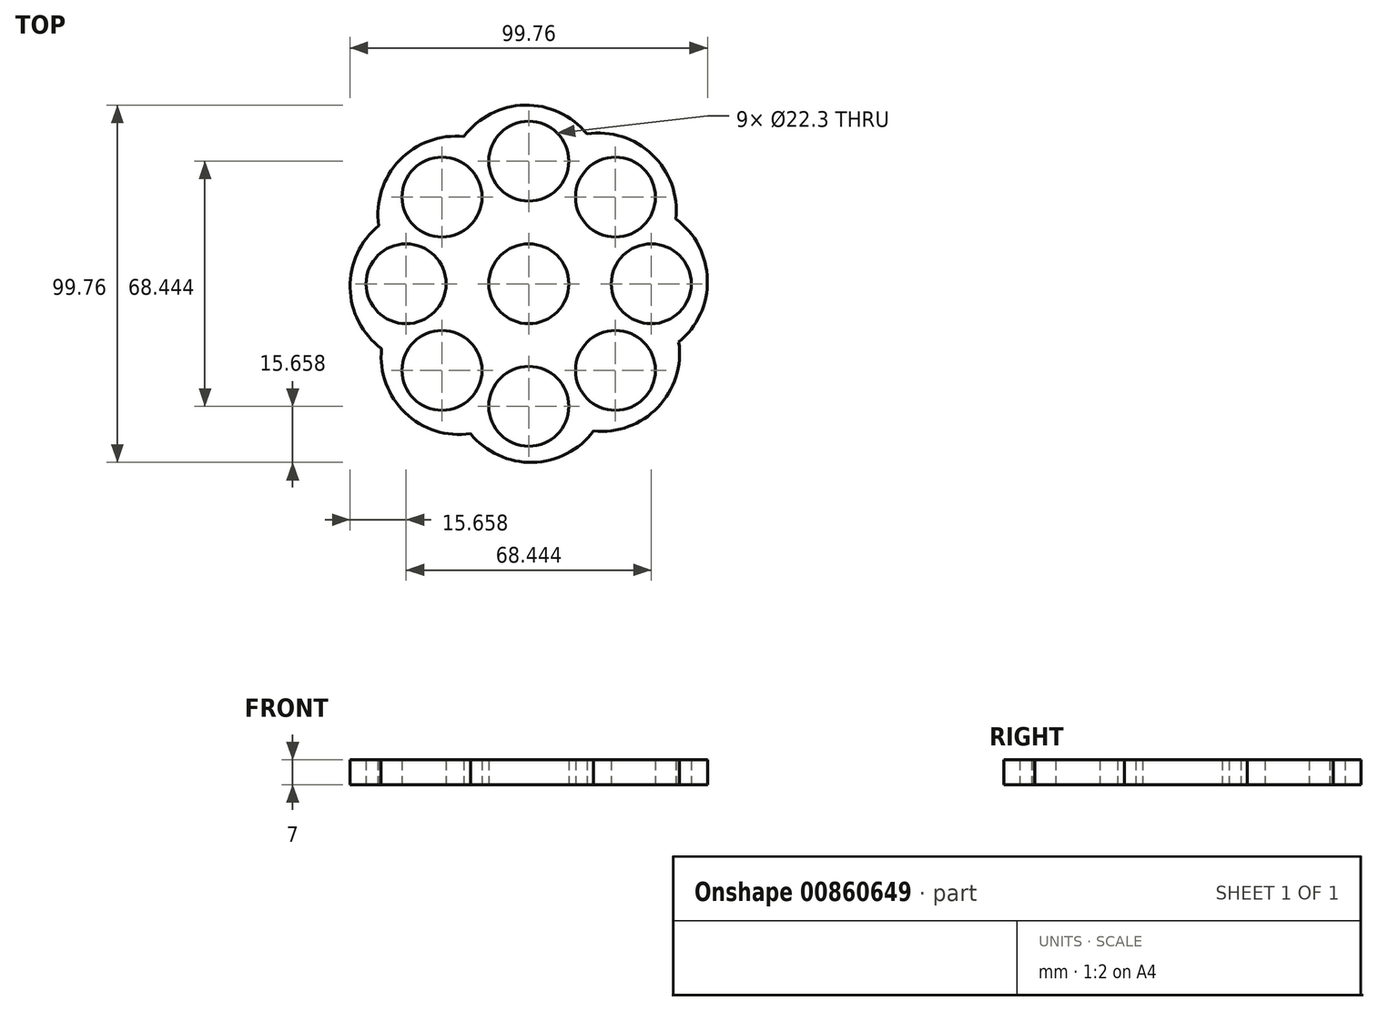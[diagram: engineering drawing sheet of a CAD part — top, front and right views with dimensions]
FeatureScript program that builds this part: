
annotation { "Feature Type Name" : "Feature", "Feature Type Description" : "" }
export const myFeature = defineFeature(function(context is Context, id is Id, definition is map)
    precondition{}
    {
        {
            var Q0;
            Q0=qCreatedBy(makeId("Top.planeOp"),FACE);
            var sketch = newSketch(context, id + "F0", { "sketchPlane" : qUnion([Q0])});
            skCircle(sketch, "E0", {"center": v(0, 0) * mm, "radius": 9.15 * mm});
            skCircle(sketch, "E1", {"center": v(0, 0) * mm, "radius": 11.15 * mm});
            skCircle(sketch, "E2", {"center": v(0, 34.22) * mm, "radius": 9.15 * mm});
            skCircle(sketch, "E3", {"center": v(0, 34.22) * mm, "radius": 11.15 * mm});
            skLineSegment(sketch, "E4.0", {"start": v(-22.6, -9.36) * mm, "end": v(-22.6, 9.36) * mm});
            skLineSegment(sketch, "E4.1", {"start": v(-22.6, 9.36) * mm, "end": v(-9.36, 22.6) * mm});
            skLineSegment(sketch, "E4.2", {"start": v(-9.36, 22.6) * mm, "end": v(9.36, 22.6) * mm});
            skLineSegment(sketch, "E4.3", {"start": v(9.36, 22.6) * mm, "end": v(22.6, 9.36) * mm});
            skLineSegment(sketch, "E4.4", {"start": v(22.6, 9.36) * mm, "end": v(22.6, -9.36) * mm});
            skLineSegment(sketch, "E4.5", {"start": v(22.6, -9.36) * mm, "end": v(9.36, -22.6) * mm});
            skLineSegment(sketch, "E4.6", {"start": v(9.36, -22.6) * mm, "end": v(-9.36, -22.6) * mm});
            skLineSegment(sketch, "E4.7", {"start": v(-9.36, -22.6) * mm, "end": v(-22.6, -9.36) * mm});
            skPoint(sketch, "E4.0.midPoint", {"position": v(-22.6, 0) * mm});
            skCircle(sketch, "E5.1.0", {"center": v(-24.2, 24.2) * mm, "radius": 9.15 * mm});
            skCircle(sketch, "E5.1.1", {"center": v(-24.2, 24.2) * mm, "radius": 11.15 * mm});
            skCircle(sketch, "E5.2.0", {"center": v(-34.22, 0) * mm, "radius": 9.15 * mm});
            skCircle(sketch, "E5.2.1", {"center": v(-34.22, 0) * mm, "radius": 11.15 * mm});
            skCircle(sketch, "E5.3.0", {"center": v(-24.2, -24.2) * mm, "radius": 9.15 * mm});
            skCircle(sketch, "E5.3.1", {"center": v(-24.2, -24.2) * mm, "radius": 11.15 * mm});
            skCircle(sketch, "E5.4.0", {"center": v(0, -34.22) * mm, "radius": 9.15 * mm});
            skCircle(sketch, "E5.4.1", {"center": v(0, -34.22) * mm, "radius": 11.15 * mm});
            skCircle(sketch, "E5.5.0", {"center": v(24.2, -24.2) * mm, "radius": 9.15 * mm});
            skCircle(sketch, "E5.5.1", {"center": v(24.2, -24.2) * mm, "radius": 11.15 * mm});
            skCircle(sketch, "E5.6.0", {"center": v(34.22, 0) * mm, "radius": 9.15 * mm});
            skCircle(sketch, "E5.6.1", {"center": v(34.22, 0) * mm, "radius": 11.15 * mm});
            skCircle(sketch, "E5.7.0", {"center": v(24.2, 24.2) * mm, "radius": 9.15 * mm});
            skCircle(sketch, "E5.7.1", {"center": v(24.2, 24.2) * mm, "radius": 11.15 * mm});
            skLineSegment(sketch, "E6", {"start": v(-9.36, 22.6) * mm, "end": v(-18.1, 41.1) * mm});
            skLineSegment(sketch, "E7.1.0", {"start": v(-22.6, 9.36) * mm, "end": v(-41.86, 16.26) * mm});
            skLineSegment(sketch, "E7.2.0", {"start": v(-22.6, -9.36) * mm, "end": v(-41.1, -18.1) * mm});
            skLineSegment(sketch, "E7.3.0", {"start": v(-9.36, -22.6) * mm, "end": v(-16.26, -41.86) * mm});
            skLineSegment(sketch, "E7.4.0", {"start": v(9.36, -22.6) * mm, "end": v(18.1, -41.1) * mm});
            skLineSegment(sketch, "E7.5.0", {"start": v(22.6, -9.36) * mm, "end": v(41.86, -16.26) * mm});
            skLineSegment(sketch, "E7.6.0", {"start": v(22.6, 9.36) * mm, "end": v(41.1, 18.1) * mm});
            skLineSegment(sketch, "E7.7.0", {"start": v(9.36, 22.6) * mm, "end": v(16.26, 41.86) * mm});
            skArc(sketch, "E8", {"start": v(16.26, 41.86) * mm, "mid": v(-1.1, 49.87) * mm, "end": v(-18.1, 41.1) * mm});
            skArc(sketch, "E9.1.0", {"start": v(-18.1, 41.1) * mm, "mid": v(-36.05, 34.48) * mm, "end": v(-41.86, 16.26) * mm});
            skArc(sketch, "E9.2.0", {"start": v(-41.86, 16.26) * mm, "mid": v(-49.87, -1.1) * mm, "end": v(-41.1, -18.1) * mm});
            skArc(sketch, "E9.3.0", {"start": v(-41.1, -18.1) * mm, "mid": v(-34.48, -36.05) * mm, "end": v(-16.26, -41.86) * mm});
            skArc(sketch, "E9.4.0", {"start": v(-16.26, -41.86) * mm, "mid": v(1.1, -49.87) * mm, "end": v(18.1, -41.1) * mm});
            skArc(sketch, "E9.5.0", {"start": v(18.1, -41.1) * mm, "mid": v(36.05, -34.48) * mm, "end": v(41.86, -16.26) * mm});
            skArc(sketch, "E9.6.0", {"start": v(41.86, -16.26) * mm, "mid": v(49.87, 1.1) * mm, "end": v(41.1, 18.1) * mm});
            skArc(sketch, "E9.7.0", {"start": v(41.1, 18.1) * mm, "mid": v(34.48, 36.05) * mm, "end": v(16.26, 41.86) * mm});
            skSolve(sketch);
        }
        {
            var Q0;
            Q0 = qSketchRegion(id + "F0", true);
            var Q1;
            Q1=makeQuery(id+"F0.imprint","IMPRINT",FACE,{"disambiguationData":[TD([[makeQuery(id+"F0.imprint","IMPRINT",EDGE,{"derivedFrom":sQuery(id+"F0.wireOp",EDGE,"E1")}),-1.0]])]});
            extrude(context, id + "F1", {"entities" : qUnion([Q0, Q1]), "depth" : 7 * mm, "offsetDistance" : 25 * mm});
        }
    });
